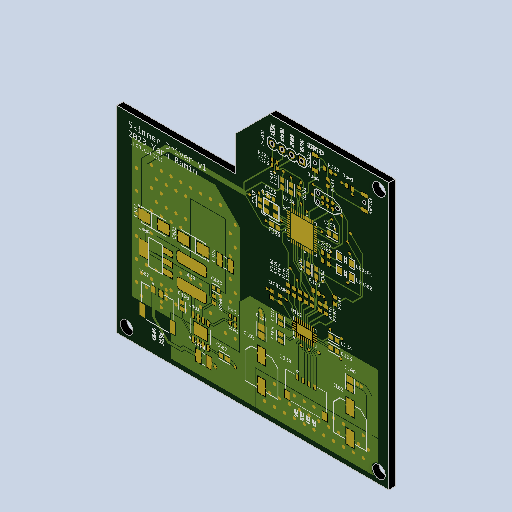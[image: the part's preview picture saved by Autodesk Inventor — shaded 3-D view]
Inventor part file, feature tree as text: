
AUTODESK INVENTOR PART (.ipt)
format: ipt  version: 2023.2 (Build 272271000, 271)  size: 937,984 bytes
history: native  units: in
note: dims shown in document units (in); Inventor stores cm internally (conversion verified against a paired STEP export)
features: hole x12, sketch x12, other x8, extrude x1
ambient origin geometry x8: Origin, YZ Plane, XZ Plane, XY Plane, X Axis, Y Axis, Z Axis, Center Point
bodies: Solid1 (feature_tree)
feature tree (33):
  other  "skimmer_swabbie_v1_BOARD"
  other  "BoardFrontPlane"
  extrude  "BoardOutline"  Depth=0.0638in
  other  "Decal_Top"
  other  "Decal_Bottom"
  hole  "SW301-H1"  [1 undecoded]
  hole  "SW300-H1"  [1 undecoded]
  hole  "Free-MNT+4"  [1 undecoded]
  hole  "Free-MNT+3"  [1 undecoded]
  hole  "Free-MNT+2"  [1 undecoded]
  hole  "JP300-1"  [1 undecoded]
  hole  "JP300-2"  [1 undecoded]
  hole  "JP300-3"  [1 undecoded]
  hole  "JP300-4"  [1 undecoded]
  hole  "J300-_OMJMIDLA"  [1 undecoded]
  hole  "J300-_YAKUTFXJ"  [1 undecoded]
  hole  "J300-_MBXSYRVB"  [1 undecoded]
  other  "img_Top"
  other  "G_247379250_TopDecalImage"
  other  "img_Bottom"
  other  "G_247379250_BottomDecalImage"
  sketch  "Sketch4"  dims[d0=0.0638in d1=0.0in d2=0.0638in]
  sketch  "Sketch5"  dims[d4=-0.0638in]
  sketch  "Sketch6"  dims[d6=0.0335in d7=0.75in d8=0.375in d9=0.25in d10=0.5635in d11=1.0in d12=0.0in]
  sketch  "Sketch7"  dims[d13=0.0335in d14=0.75in d15=0.375in d16=0.25in d17=0.5635in d18=1.0in d19=0.0in]
  sketch  "Sketch8"  dims[d20=0.128in d21=0.75in d22=0.375in d23=0.25in d24=0.5635in d25=1.0in d26=0.0in]
  sketch  "Sketch9"  dims[d27=0.128in d28=0.75in d29=0.375in d30=0.25in d31=0.5635in d32=1.0in d33=0.0in]
  sketch  "Sketch10"  dims[d34=0.128in d35=0.75in d36=0.375in d37=0.25in d38=0.5635in d39=1.0in d40=0.0in]
  sketch  "Sketch11"  dims[d41=0.04in d42=0.75in d43=0.375in d44=0.25in d45=0.5635in d46=1.0in d47=0.0in]
  sketch  "Sketch12"  dims[d48=0.04in d49=0.75in d50=0.375in d51=0.25in d52=0.5635in d53=1.0in d54=0.0in]
  sketch  "Sketch13"  dims[d55=0.04in d56=0.75in d57=0.375in d58=0.25in d59=0.5635in d60=1.0in d61=0.0in]
  sketch  "Sketch14"  dims[d62=0.04in d63=0.75in d64=0.375in d65=0.25in d66=0.5635in d67=1.0in d68=0.0in]
  sketch  "Sketch15"  dims[d69=0.0354in d70=0.75in d71=0.375in d72=0.25in d73=0.5635in d74=1.0in d75=0.0in d76=0.0354in d77=0.75in d78=0.375in d79=0.25in d80=0.5635in d81=1.0in d82=0.0in d83=0.0354in d84=0.75in d85=0.375in d86=0.25in d87=0.5635in d88=1.0in d89=0.0in]
note: 12 required parameter values undecoded (feature->parameter linkage not recoverable at this tier; creation-order binding heuristic only, values carry confidence <= 0.55)
